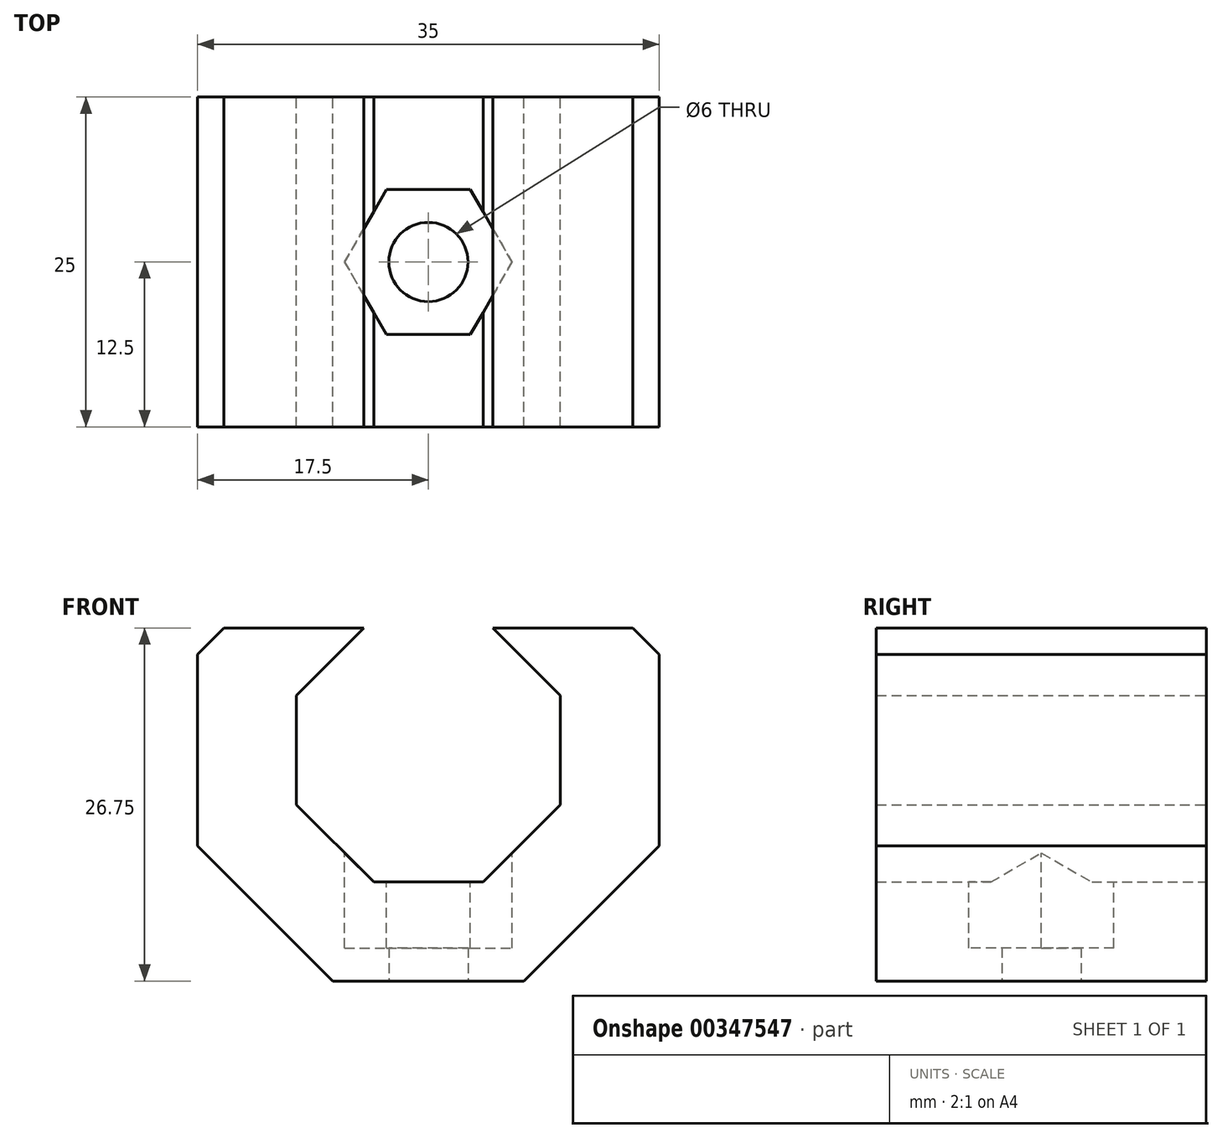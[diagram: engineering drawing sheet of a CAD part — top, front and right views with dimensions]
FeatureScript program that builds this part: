
annotation { "Feature Type Name" : "Feature", "Feature Type Description" : "" }
export const myFeature = defineFeature(function(context is Context, id is Id, definition is map)
    precondition{}
    {
        {
            var Q0;
            Q0=qCreatedBy(makeId("Front.planeOp"),FACE);
            var sketch = newSketch(context, id + "F0", { "sketchPlane" : qUnion([Q0])});
            skCircle(sketch, "E0.cCircle", {"center": v(0, 0) * mm, "radius": 10 * mm, "construction": true});
            skLineSegment(sketch, "E0.0", {"start": v(10, 4.14) * mm, "end": v(10, -4.14) * mm});
            skLineSegment(sketch, "E0.1", {"start": v(10, -4.14) * mm, "end": v(4.14, -10) * mm});
            skLineSegment(sketch, "E0.2", {"start": v(4.14, -10) * mm, "end": v(-4.14, -10) * mm});
            skLineSegment(sketch, "E0.3", {"start": v(-4.14, -10) * mm, "end": v(-10, -4.14) * mm});
            skLineSegment(sketch, "E0.4", {"start": v(-10, -4.14) * mm, "end": v(-10, 4.14) * mm});
            skLineSegment(sketch, "E0.5", {"start": v(-10, 4.14) * mm, "end": v(-4.14, 10) * mm});
            skLineSegment(sketch, "E0.6", {"start": v(-4.14, 10) * mm, "end": v(4.14, 10) * mm});
            skLineSegment(sketch, "E0.7", {"start": v(4.14, 10) * mm, "end": v(10, 4.14) * mm});
            skPoint(sketch, "E0.0.midPoint", {"position": v(10, 0) * mm});
            skCircle(sketch, "E1.cCircle", {"center": v(0, 0) * mm, "radius": 17.5 * mm, "construction": true});
            skLineSegment(sketch, "E1.0", {"start": v(17.5, 7.25) * mm, "end": v(17.5, -7.25) * mm});
            skLineSegment(sketch, "E1.1", {"start": v(17.5, -7.25) * mm, "end": v(7.25, -17.5) * mm});
            skLineSegment(sketch, "E1.2", {"start": v(7.25, -17.5) * mm, "end": v(-7.25, -17.5) * mm});
            skLineSegment(sketch, "E1.3", {"start": v(-7.25, -17.5) * mm, "end": v(-17.5, -7.25) * mm});
            skLineSegment(sketch, "E1.4", {"start": v(-17.5, -7.25) * mm, "end": v(-17.5, 7.25) * mm});
            skLineSegment(sketch, "E1.5", {"start": v(-17.5, 7.25) * mm, "end": v(-7.25, 17.5) * mm});
            skLineSegment(sketch, "E1.6", {"start": v(-7.25, 17.5) * mm, "end": v(7.25, 17.5) * mm});
            skLineSegment(sketch, "E1.7", {"start": v(7.25, 17.5) * mm, "end": v(17.5, 7.25) * mm});
            skPoint(sketch, "E1.0.midPoint", {"position": v(17.5, 0) * mm});
            skSolve(sketch);
        }
        {
            var Q0;
            Q0 = qSketchRegion(id + "F0", true);
            extrude(context, id + "F1", {"entities" : qUnion([Q0]), "depth" : 25 * mm});
        }
        {
            var Q0;
            Q0=makeQuery(id+"F1.opExtrude","CAP_FACE",FACE,{"disambiguationData":[OSD([sQuery(id+"F0.wireOp",EDGE,"E0.0"),sQuery(id+"F0.wireOp",EDGE,"E0.1"),sQuery(id+"F0.wireOp",EDGE,"E0.2"),sQuery(id+"F0.wireOp",EDGE,"E0.3"),sQuery(id+"F0.wireOp",EDGE,"E0.4"),sQuery(id+"F0.wireOp",EDGE,"E0.5"),sQuery(id+"F0.wireOp",EDGE,"E0.6"),sQuery(id+"F0.wireOp",EDGE,"E0.7"),sQuery(id+"F0.wireOp",EDGE,"E1.0"),sQuery(id+"F0.wireOp",EDGE,"E1.1"),sQuery(id+"F0.wireOp",EDGE,"E1.2"),sQuery(id+"F0.wireOp",EDGE,"E1.3"),sQuery(id+"F0.wireOp",EDGE,"E1.4"),sQuery(id+"F0.wireOp",EDGE,"E1.5"),sQuery(id+"F0.wireOp",EDGE,"E1.6"),sQuery(id+"F0.wireOp",EDGE,"E1.7")])],"isStart":false});
            var sketch = newSketch(context, id + "F2", { "sketchPlane" : qUnion([Q0])});
            skLineSegment(sketch, "E2.bottom", {"start": v(-17.5, 19.25) * mm, "end": v(17.5, 19.25) * mm});
            skLineSegment(sketch, "E2.top", {"start": v(-17.5, 9.25) * mm, "end": v(17.5, 9.25) * mm});
            skLineSegment(sketch, "E2.left", {"start": v(-17.5, 19.25) * mm, "end": v(-17.5, 9.25) * mm});
            skLineSegment(sketch, "E2.right", {"start": v(17.5, 19.25) * mm, "end": v(17.5, 9.25) * mm});
            skSolve(sketch);
        }
        {
            var Q0;
            Q0 = qSketchRegion(id + "F2", true);
            extrude(context, id + "F3", {"entities" : qUnion([Q0]), "operationType" : NewBodyOperationType.REMOVE, "oppositeDirection" : true, "depth" : 40 * mm});
        }
        {
            var Q0;
            Q0=makeQuery(id+"F1.opExtrude","SWEPT_FACE",FACE,{"disambiguationData":[OSD([sQuery(id+"F0.wireOp",EDGE,"E0.2")])]});
            var sketch = newSketch(context, id + "F4", { "sketchPlane" : qUnion([Q0])});
            skCircle(sketch, "E3.cCircle", {"center": v(0, -12.5) * mm, "radius": 5.5 * mm, "construction": true});
            skLineSegment(sketch, "E3.0", {"start": v(-3.18, -7) * mm, "end": v(3.18, -7) * mm});
            skLineSegment(sketch, "E3.1", {"start": v(3.18, -7) * mm, "end": v(6.35, -12.5) * mm});
            skLineSegment(sketch, "E3.2", {"start": v(6.35, -12.5) * mm, "end": v(3.18, -18) * mm});
            skLineSegment(sketch, "E3.3", {"start": v(3.18, -18) * mm, "end": v(-3.18, -18) * mm});
            skLineSegment(sketch, "E3.4", {"start": v(-3.18, -18) * mm, "end": v(-6.35, -12.5) * mm});
            skLineSegment(sketch, "E3.5", {"start": v(-6.35, -12.5) * mm, "end": v(-3.18, -7) * mm});
            skPoint(sketch, "E3.0.midPoint", {"position": v(0, -7) * mm});
            skSolve(sketch);
        }
        {
            var Q0;
            Q0 = qSketchRegion(id + "F4", true);
            extrude(context, id + "F5", {"entities" : qUnion([Q0]), "operationType" : NewBodyOperationType.REMOVE, "oppositeDirection" : true, "depth" : 5 * mm, "hasSecondDirection" : true, "secondDirectionOppositeDirection" : false, "secondDirectionDepth" : 5 * mm});
        }
        {
            var Q0;
            Q0=makeQuery(id+"F1.opExtrude","SWEPT_FACE",FACE,{"disambiguationData":[OSD([sQuery(id+"F0.wireOp",EDGE,"E1.2")])]});
            var sketch = newSketch(context, id + "F6", { "sketchPlane" : qUnion([Q0])});
            skCircle(sketch, "E4", {"center": v(0, 12.5) * mm, "radius": 3 * mm});
            skLineSegment(sketch, "E5", {"start": v(0, 25) * mm, "end": v(0, 0) * mm, "construction": true});
            skSolve(sketch);
        }
        {
            var Q0;
            Q0 = qSketchRegion(id + "F6", true);
            extrude(context, id + "F7", {"entities" : qUnion([Q0]), "operationType" : NewBodyOperationType.REMOVE, "oppositeDirection" : true, "depth" : 25 * mm});
        }
    });
